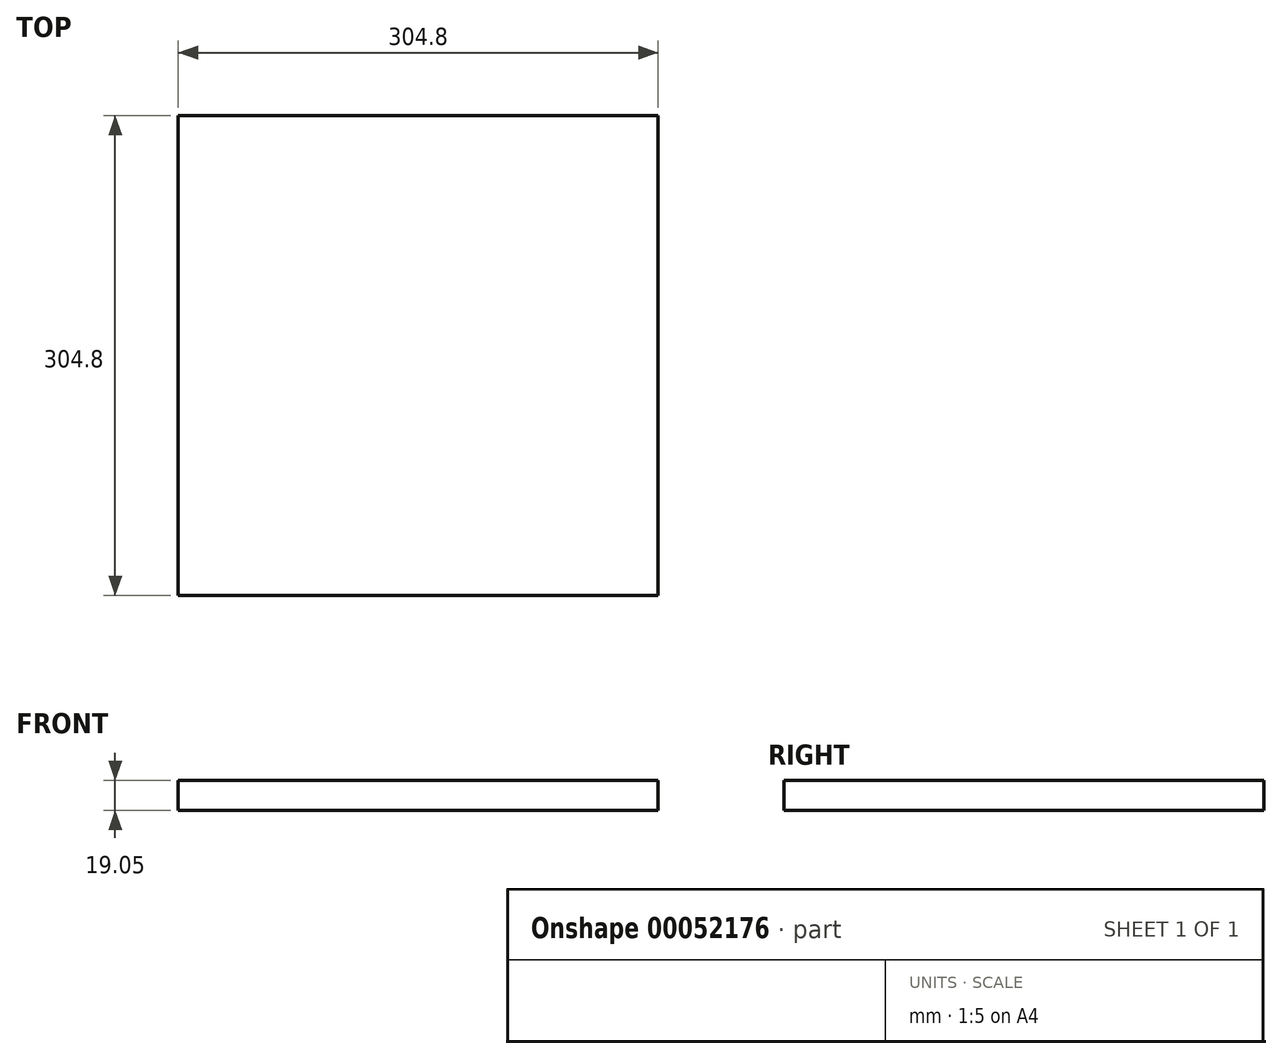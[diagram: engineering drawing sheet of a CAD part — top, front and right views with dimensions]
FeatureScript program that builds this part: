
annotation { "Feature Type Name" : "Feature", "Feature Type Description" : "" }
export const myFeature = defineFeature(function(context is Context, id is Id, definition is map)
    precondition{}
    {
        {
            var Q0;
            Q0=qCreatedBy(makeId("Top.planeOp"),FACE);
            var sketch = newSketch(context, id + "F0", { "sketchPlane" : qUnion([Q0])});
            skLineSegment(sketch, "E0.rect.bottom", {"start": v(152.4, 152.4) * mm, "end": v(-152.4, 152.4) * mm});
            skLineSegment(sketch, "E0.rect.top", {"start": v(152.4, -152.4) * mm, "end": v(-152.4, -152.4) * mm});
            skLineSegment(sketch, "E0.rect.left", {"start": v(152.4, 152.4) * mm, "end": v(152.4, -152.4) * mm});
            skLineSegment(sketch, "E0.rect.right", {"start": v(-152.4, 152.4) * mm, "end": v(-152.4, -152.4) * mm});
            skPoint(sketch, "E0.rect.middle", {"position": v(0, 0) * mm});
            skSolve(sketch);
        }
        {
            var Q0;
            Q0=makeQuery(id+"F0.imprint","IMPRINT",FACE,{"disambiguationData":[TD([[makeQuery(id+"F0.imprint","IMPRINT",EDGE,{"derivedFrom":sQuery(id+"F0.wireOp",EDGE,"E0.rect.bottom")}),1.0]])]});
            extrude(context, id + "F1", {"entities" : qUnion([Q0]), "depth" : 19.05 * mm});
        }
    });
